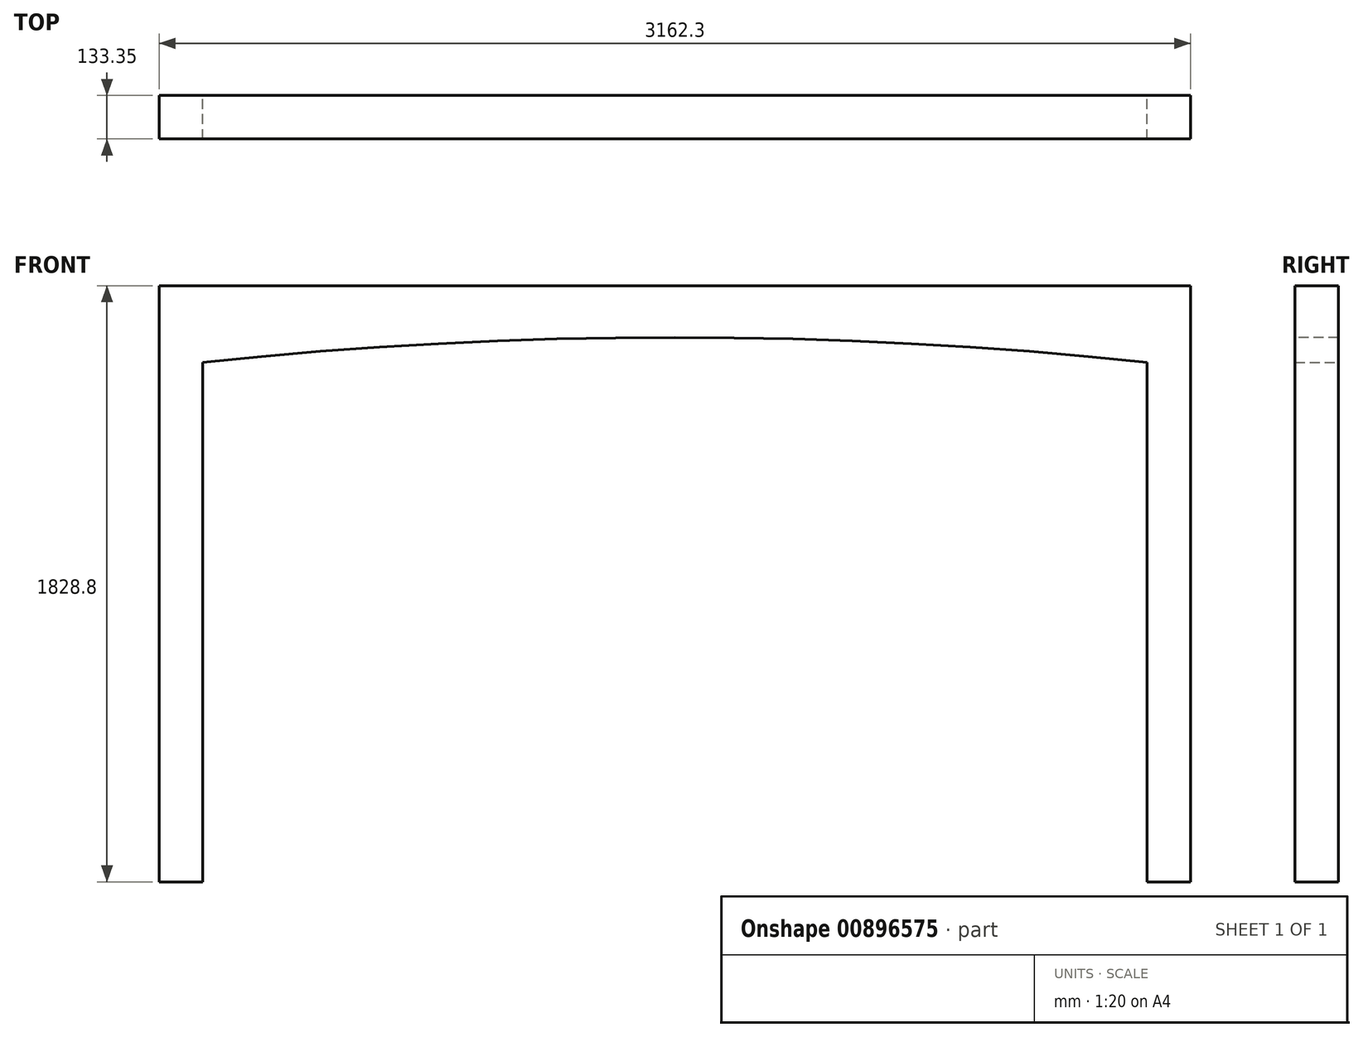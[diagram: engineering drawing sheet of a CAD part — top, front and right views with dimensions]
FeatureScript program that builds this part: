
annotation { "Feature Type Name" : "Feature", "Feature Type Description" : "" }
export const myFeature = defineFeature(function(context is Context, id is Id, definition is map)
    precondition{}
    {
        {
            var Q0;
            Q0=qCreatedBy(makeId("Front.planeOp"),FACE);
            var sketch = newSketch(context, id + "F0", { "sketchPlane" : qUnion([Q0])});
            skLineSegment(sketch, "E0.bottom", {"start": v(0, 0) * mm, "end": v(133.35, 0) * mm});
            skLineSegment(sketch, "E0.top", {"start": v(0, 1828.8) * mm, "end": v(133.35, 1828.8) * mm});
            skLineSegment(sketch, "E0.left", {"start": v(0, 0) * mm, "end": v(0, 1828.8) * mm});
            skLineSegment(sketch, "E0.right", {"start": v(133.35, 0) * mm, "end": v(133.35, 1828.8) * mm});
            skLineSegment(sketch, "E1.bottom", {"start": v(3028.95, 0) * mm, "end": v(3162.3, 0) * mm});
            skLineSegment(sketch, "E1.top", {"start": v(3028.95, 1828.8) * mm, "end": v(3162.3, 1828.8) * mm});
            skLineSegment(sketch, "E1.left", {"start": v(3028.95, 0) * mm, "end": v(3028.95, 1828.8) * mm});
            skLineSegment(sketch, "E1.right", {"start": v(3162.3, 0) * mm, "end": v(3162.3, 1828.8) * mm});
            skLineSegment(sketch, "E2", {"start": v(133.35, 1828.8) * mm, "end": v(3028.95, 1828.8) * mm});
            skLineSegment(sketch, "E3", {"start": v(133.35, 1593.85) * mm, "end": v(3028.95, 1593.85) * mm});
            skSolve(sketch);
        }
        {
            var Q0;
            Q0 = qSketchRegion(id + "F0", true);
            extrude(context, id + "F1", {"entities" : qUnion([Q0]), "depth" : 133.35 * mm, "offsetDistance" : 25.4 * mm});
        }
        {
            var Q0;
            Q0=makeQuery(id+"F1.opExtrude","CAP_FACE",FACE,{"disambiguationData":[OSD([sQuery(id+"F0.wireOp",EDGE,"E0.bottom"),sQuery(id+"F0.wireOp",EDGE,"E0.top"),sQuery(id+"F0.wireOp",EDGE,"E0.left"),sQuery(id+"F0.wireOp",EDGE,"E0.right"),sQuery(id+"F0.wireOp",EDGE,"E1.bottom"),sQuery(id+"F0.wireOp",EDGE,"E1.top"),sQuery(id+"F0.wireOp",EDGE,"E1.left"),sQuery(id+"F0.wireOp",EDGE,"E1.right"),sQuery(id+"F0.wireOp",EDGE,"E2"),sQuery(id+"F0.wireOp",EDGE,"E3")])],"isStart":false});
            var sketch = newSketch(context, id + "F2", { "sketchPlane" : qUnion([Q0])});
            skArc(sketch, "E4", {"start": v(3028.95, 1593.85) * mm, "mid": v(1581.15, 1670.05) * mm, "end": v(133.35, 1593.85) * mm});
            skLineSegment(sketch, "E5", {"start": v(3028.95, 1593.85) * mm, "end": v(133.35, 1593.85) * mm});
            skSolve(sketch);
        }
        {
            var Q0;
            Q0 = qSketchRegion(id + "F2", true);
            extrude(context, id + "F3", {"entities" : qUnion([Q0]), "operationType" : NewBodyOperationType.REMOVE, "endBound" : BoundingType.THROUGH_ALL, "oppositeDirection" : true, "depth" : 25.4 * mm, "offsetDistance" : 25.4 * mm});
        }
    });
